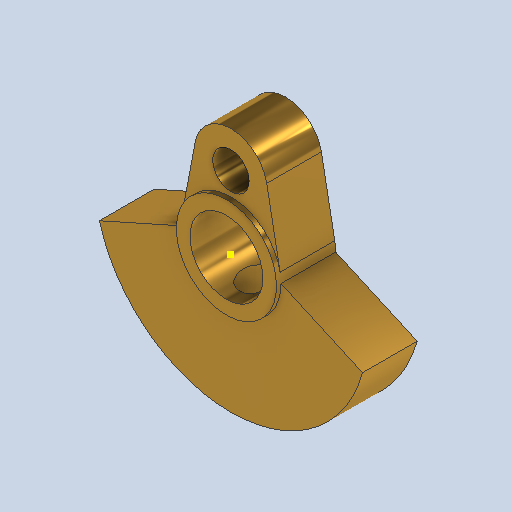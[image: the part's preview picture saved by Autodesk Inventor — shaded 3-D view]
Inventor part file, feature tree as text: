
AUTODESK INVENTOR PART (.ipt)
format: ipt  version: 2022 (Build 260153000, 153)  size: 180,736 bytes
history: native  units: mm
features: sketch x7, hole x3, extrude x2, plane x1
ambient origin geometry x8: Origin, YZ Plane, XZ Plane, XY Plane, X Axis, Y Axis, Z Axis, Center Point
bodies: Solid1 (feature_tree)
feature tree (13):
  sketch  "Sketch1"  dims[d0=30.0mm d1=11.0mm]
  extrude  "Extrusion1"  Depth=11.0mm
  sketch  "Sketch2"  dims[d2=4.0mm d3=8.0mm]
  extrude  "Extrusion2"  Depth=4.0mm
  hole  "Hole2"  [1 undecoded]
  sketch  "Sketch4"  dims[d6=6.0mm d7=0.0mm d8=0.5mm d9=0.0mm]
  sketch  "3D Sketch1"
  plane  "Work Plane1"
  hole  "Hole3"  [1 undecoded]
  hole  "Hole4"  [1 undecoded]
  sketch  "Sketch3"  dims[d4=4.0mm d5=8.0mm]
  sketch  "Sketch5"  dims[d17=8.0mm d18=6.0mm d19=4.0mm d20=2.0mm d21=90.0deg d22=3.0mm d23=20.594885mm d26=3.0mm]
  sketch  "Sketch6"  dims[d27=4.0mm d28=6.0mm d29=4.0mm d30=2.0mm d31=90.0deg d32=11.0mm d33=20.594885mm d34=4.0mm d35=6.0mm d36=4.0mm d37=2.0mm d38=90.0deg d39=11.0mm d40=20.594885mm]
note: 3 required parameter values undecoded (feature->parameter linkage not recoverable at this tier; creation-order binding heuristic only, values carry confidence <= 0.55)
